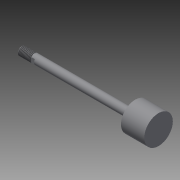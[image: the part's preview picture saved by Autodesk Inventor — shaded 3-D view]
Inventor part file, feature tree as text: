
AUTODESK INVENTOR PART (.ipt)
format: ipt  version: 2014 SP2 (Build 180246200, 246)  size: 161,792 bytes
history: native  units: in
note: dims shown in document units (in); Inventor stores cm internally (conversion verified against a paired STEP export)
features: other x112, sketch x3, revolve x2, thread x1, extrude x1
ambient origin geometry x8: Origin, YZ Plane, XZ Plane, XY Plane, X Axis, Y Axis, Z Axis, Center Point
bodies: Solid1 (feature_tree)
feature tree (119):
  revolve  "Revolution1"  Angle=360.0deg
  revolve  "Revolution2"  [1 undecoded]
  thread  "Thread1"  [1 undecoded]
  extrude  "Extrusion1"  [1 undecoded]
  other  "dia1_XY"
  other  "dia1_YZ"
  other  "dia1_ZX"
  other  "dia1_X"
  other  "dia1_Y"
  other  "dia1_Z"
  other  "dia1_Center"
  other  "dia12_XY"
  other  "dia12_YZ"
  other  "dia12_ZX"
  other  "dia12_X"
  other  "dia12_Y"
  other  "dia12_Z"
  other  "dia12_Center"
  other  "dia2_XY"
  other  "dia2_YZ"
  other  "dia2_ZX"
  other  "dia2_X"
  other  "dia2_Y"
  other  "dia2_Z"
  other  "dia2_Center"
  other  "dia22_XY"
  other  "dia22_YZ"
  other  "dia22_ZX"
  other  "dia22_X"
  other  "dia22_Y"
  other  "dia22_Z"
  other  "dia22_Center"
  other  "hh1_XY"
  other  "hh1_YZ"
  other  "hh1_ZX"
  other  "hh1_X"
  other  "hh1_Y"
  other  "hh1_Z"
  other  "hh1_Center"
  other  "hh2_XY"
  other  "hh2_YZ"
  other  "hh2_ZX"
  other  "hh2_X"
  other  "hh2_Y"
  other  "hh2_Z"
  other  "hh2_Center"
  other  "rl1_XY"
  other  "rl1_YZ"
  other  "rl1_ZX"
  other  "rl1_X"
  other  "rl1_Y"
  other  "rl1_Z"
  other  "rl1_Center"
  other  "rl2_XY"
  other  "rl2_YZ"
  other  "rl2_ZX"
  other  "rl2_X"
  other  "rl2_Y"
  other  "rl2_Z"
  other  "rl2_Center"
  other  "rod_cp_XY"
  other  "rod_cp_YZ"
  other  "rod_cp_ZX"
  other  "rod_cp_X"
  other  "rod_cp_Y"
  other  "rod_cp_Z"
  other  "rod_cp_Center"
  other  "thd1_XY"
  other  "thd1_YZ"
  other  "thd1_ZX"
  other  "thd1_X"
  other  "thd1_Y"
  other  "thd1_Z"
  other  "thd1_Center"
  other  "thd2_XY"
  other  "thd2_YZ"
  other  "thd2_ZX"
  other  "thd2_X"
  other  "thd2_Y"
  other  "thd2_Z"
  other  "thd2_Center"
  other  "to_rod_clevis_XY"
  other  "to_rod_clevis_YZ"
  other  "to_rod_clevis_ZX"
  other  "to_rod_clevis_X"
  other  "to_rod_clevis_Y"
  other  "to_rod_clevis_Z"
  other  "to_rod_clevis_Center"
  other  "wf1_XY"
  other  "wf1_YZ"
  other  "wf1_ZX"
  other  "wf1_X"
  other  "wf1_Y"
  other  "wf1_Z"
  other  "wf1_Center"
  other  "wf2_XY"
  other  "wf2_YZ"
  other  "wf2_ZX"
  other  "wf2_X"
  other  "wf2_Y"
  other  "wf2_Z"
  other  "wf2_Center"
  other  "wfw1_XY"
  other  "wfw1_YZ"
  other  "wfw1_ZX"
  other  "wfw1_X"
  other  "wfw1_Y"
  other  "wfw1_Z"
  other  "wfw1_Center"
  other  "wfw2_XY"
  other  "wfw2_YZ"
  other  "wfw2_ZX"
  other  "wfw2_X"
  other  "wfw2_Y"
  other  "wfw2_Z"
  other  "wfw2_Center"
  sketch  "Sketch_1"  dims[d0=360.0deg d1=360.0deg]
  sketch  "Sketch_3"  dims[d2=0.4752in d3=0.0in d4=0.125in d5=0.0in]
  sketch  "Sketch_10"  dims[d6=0.0in d7=0.0in d8=0.0in d9=0.0in d10=0.0in d11=0.0in d12=0.0in]
note: 3 required parameter values undecoded (feature->parameter linkage not recoverable at this tier; creation-order binding heuristic only, values carry confidence <= 0.55)